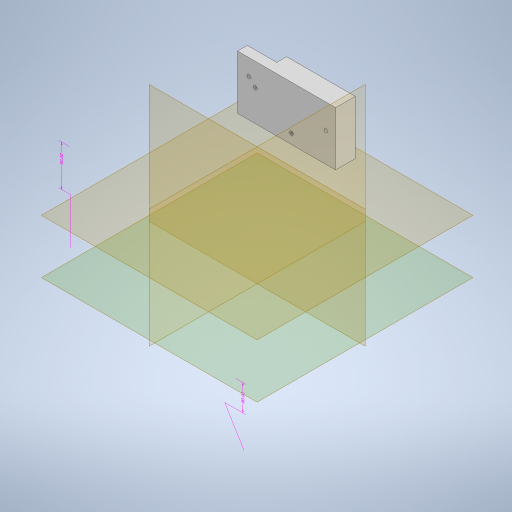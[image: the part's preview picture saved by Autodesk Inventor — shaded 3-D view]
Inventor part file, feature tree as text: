
AUTODESK INVENTOR PART (.ipt)
format: ipt  version: 2023 (Build 270158000, 158)  size: 436,224 bytes
history: native  units: mm
features: sketch x9, other x5, extrude x5, hole x4, plane x4, split x3
ambient origin geometry x8: Origin, YZ Plane, XZ Plane, XY Plane, X Axis, Y Axis, Z Axis, Center Point
bodies: Body1 (feature_tree)
feature tree (30):
  other  "Sólido1"
  other  "Anotaciones"
  extrude  "Extrusión1"  Depth=200.0mm
  hole  "Agujero1"  [1 undecoded]
  extrude  "Extrusión2"  Depth=15.0mm
  extrude  "Extrusión3"  Depth=20.0mm TaperAngle=0.0deg
  extrude  "Extrusión4"  Depth=200.0mm
  extrude  "Extrusión5"  Depth=20.0mm
  hole  "Agujero2"  [1 undecoded]
  plane  "Plano de trabajo1"
  split  "Dividir1"
  plane  "Plano de trabajo2"
  plane  "Plano de trabajo3"
  sketch  "Boceto9"  dims[d37=20.0mm d38=20.0mm]
  plane  "Plano de trabajo4"
  hole  "Agujero3"  [1 undecoded]
  hole  "Agujero4"  [1 undecoded]
  split  "Dividir2"
  split  "Dividir3"
  other  "Suprimir cara6"
  sketch  "Boceto2"  dims[d7=15.0mm d8=200.0mm]
  sketch  "Boceto3"  dims[d9=10.0mm d10=0.0mm]
  sketch  "Boceto4"  dims[d12=1.75mm d13=1.75mm d14=1.75mm d15=1.75mm d16=10.0mm d17=10.0mm d19=30.0mm]
  sketch  "Boceto5"  dims[d20=3.5mm d21=6.0mm d22=4.0mm d23=2.0mm d24=90.0deg d25=8.0mm d26=20.594885mm d27=15.0mm]
  sketch  "Boceto6"  dims[d28=20.0mm d29=80.0mm d30=0.0mm]
  sketch  "Boceto7"  dims[d31=48.0mm d32=200.0mm]
  sketch  "Boceto8"  dims[d33=110.0mm d34=0.0mm d36=20.0mm]
  sketch  "Boceto10"  dims[d39=90.0mm d40=0.0mm d42=10.0mm d43=30.0mm d44=0.0mm d46=1.75mm d47=1.75mm d48=1.75mm d49=1.75mm d50=10.0mm d51=10.0mm d52=15.0mm d56=3.5mm d57=6.0mm d58=4.0mm d59=2.0mm d60=90.0deg d61=8.0mm d62=20.594885mm d63=10.0mm d65=10.0mm d66=10.0mm d67=31.75mm d70=15.0mm d74=200.0mm d78=20.0mm d82=90.0deg d83=10.0mm d84=30.0mm d85=5.0mm d86=5.0mm d87=5.0mm d88=5.0mm d89=20.0mm d91=30.0mm d92=5.0mm d93=5.0mm d94=3.5mm d95=5.0mm d96=5.0mm d97=5.0mm d98=5.0mm d99=5.0mm d100=20.0mm d101=3.5mm d102=6.0mm d103=4.0mm d104=2.0mm d105=90.0deg d106=8.0mm d107=20.594885mm d108=10.0mm d109=30.0mm d110=5.0mm d111=5.0mm d112=5.0mm d113=5.0mm d114=5.0mm d115=5.0mm d116=3.5mm d117=5.0mm d118=5.0mm d119=5.0mm d120=5.0mm d121=5.0mm d122=30.0mm d123=30.0mm d124=3.5mm d125=6.0mm d126=4.0mm d127=2.0mm d128=90.0deg d129=8.0mm d130=20.594885mm d75=1.454734mm d76=6.982969mm d77=80.0mm d79=4.097996mm d80=1.406125mm d81=90.0mm]
  other  "Cota lineal 2"
  other  "Cota lineal 3"
note: 4 required parameter values undecoded (feature->parameter linkage not recoverable at this tier; creation-order binding heuristic only, values carry confidence <= 0.55)
